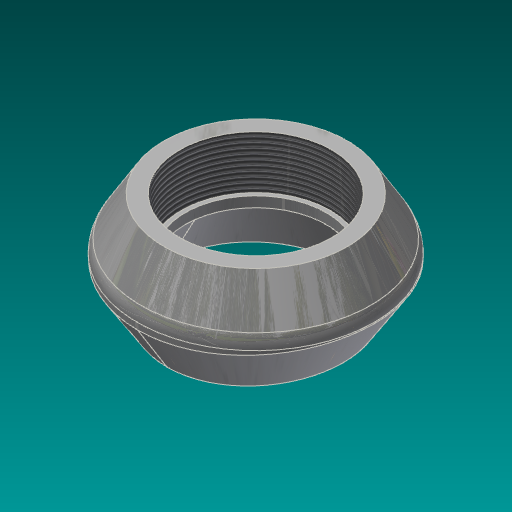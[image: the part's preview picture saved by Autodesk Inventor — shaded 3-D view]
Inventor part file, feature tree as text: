
AUTODESK INVENTOR PART (.ipt)
format: ipt  version: 2017.3 (Build 213257000, 257)  size: 449,024 bytes
history: native  units: mm (DEFAULTED — no unit token found)
features: other x8, sketch x5, plane x1, extrude x1, revolve x1, thread x1, sweep x1
ambient origin geometry x8: Origin, YZ Plane, XZ Plane, XY Plane, X Axis, Y Axis, Z Axis, Center Point
bodies: Solid1 (feature_tree)
feature tree (18):
  sketch  "Sketch1"  dims[d5=38.1mm d8=90.0deg]
  plane  "Work Plane1"
  sketch  "Sketch2"  dims[d9=0.0mm d10=917.575mm d11=10.0mm d12=0.0mm]
  extrude  "Extrusion1"  TaperAngle=90.0deg  [1 undecoded]
  revolve  "Revolution2"  [1 undecoded]
  thread  "Thread1"  [1 undecoded]
  other  "Work Point1"
  sweep  "Sweep1"
  other  "Work Axis3"
  other  "Work Point2"
  other  "Work Point3"
  sketch  "Sketch3"  dims[d45=8.810625mm d52=88.10625mm]
  sketch  "Sketch4"  dims[d54=1185.06875mm d77=68.1482mm d80=38.1mm d81=19.2151mm d83=56.55818mm d85=0.312398mm d86=90.0deg d91=52.5018mm d92=6.0mm d93=4.0mm d94=2.0mm d95=90.0deg d96=3.84302mm d97=0.0mm d102=10.0mm d103=0.0mm d106=19.05mm d107=496.8875mm d120=-458.7875mm d121=0.0mm d129=0.78232mm d130=0.78232mm d131=30.0deg d132=11.509375mm d133=0.0mm d134=0.0mm d135=90.0deg d136=0.0mm d137=90.0deg d138=65.0875mm d139=58.3692mm d140=0.0mm]
  other  "Work Axis2"
  sketch  "3D Sketch1"
  other  "Edges14"
  other  "Edges15"
  other  "Work Axis4"
note: 3 required parameter values undecoded (feature->parameter linkage not recoverable at this tier; creation-order binding heuristic only, values carry confidence <= 0.55)